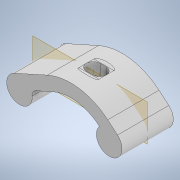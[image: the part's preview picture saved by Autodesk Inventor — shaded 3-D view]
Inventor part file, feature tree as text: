
AUTODESK INVENTOR PART (.ipt)
format: ipt  version: 2020 (Build 240168000, 168)  size: 232,960 bytes
history: native  units: in
note: dims shown in document units (in); Inventor stores cm internally (conversion verified against a paired STEP export)
features: extrude x4, sketch x4, fillet x3, projected_geometry x3, other x2, plane x1, chamfer x1
ambient origin geometry x8: Origin, YZ Plane, XZ Plane, XY Plane, X Axis, Y Axis, Z Axis, Center Point
bodies: Solid1 (feature_tree)
feature tree (18):
  extrude  "Extrusion1"  Depth=1.0in
  fillet  "Fillet1"  Radius=0.25in
  extrude  "Extrusion2"  Depth=0.5in
  plane  "Work Plane1"
  extrude  "Extrusion3"  Depth=0.125in
  fillet  "Fillet2"  Radius=0.1328in
  extrude  "Extrusion4"  Depth=0.5in
  fillet  "Fillet3"  Radius=0.507in
  chamfer  "Chamfer1"  Distance=0.2906in
  sketch  "Sketch1"  dims[d0=0.75in d1=1.0in d3=0.25in]
  sketch  "Sketch2"  dims[d5=0.5in d6=0.25in]
  other  "Work Axis1"
  other  "Work Axis2"
  sketch  "Sketch4"  dims[d7=1.0in d8=0.0in d9=0.125in d12=0.1328in]
  sketch  "Sketch5"  dims[d13=0.125in d14=0.5in d15=0.507in d16=0.0in d17=0.2906in d18=0.0in d19=0.125in d20=0.2906in d21=0.0in d22=0.125in d23=0.02in d24=0.125in d25=45.0deg]
  projected_geometry  "Projected Loop1"
  projected_geometry  "Project Cut Edges1"
  projected_geometry  "Project Cut Edges2"
